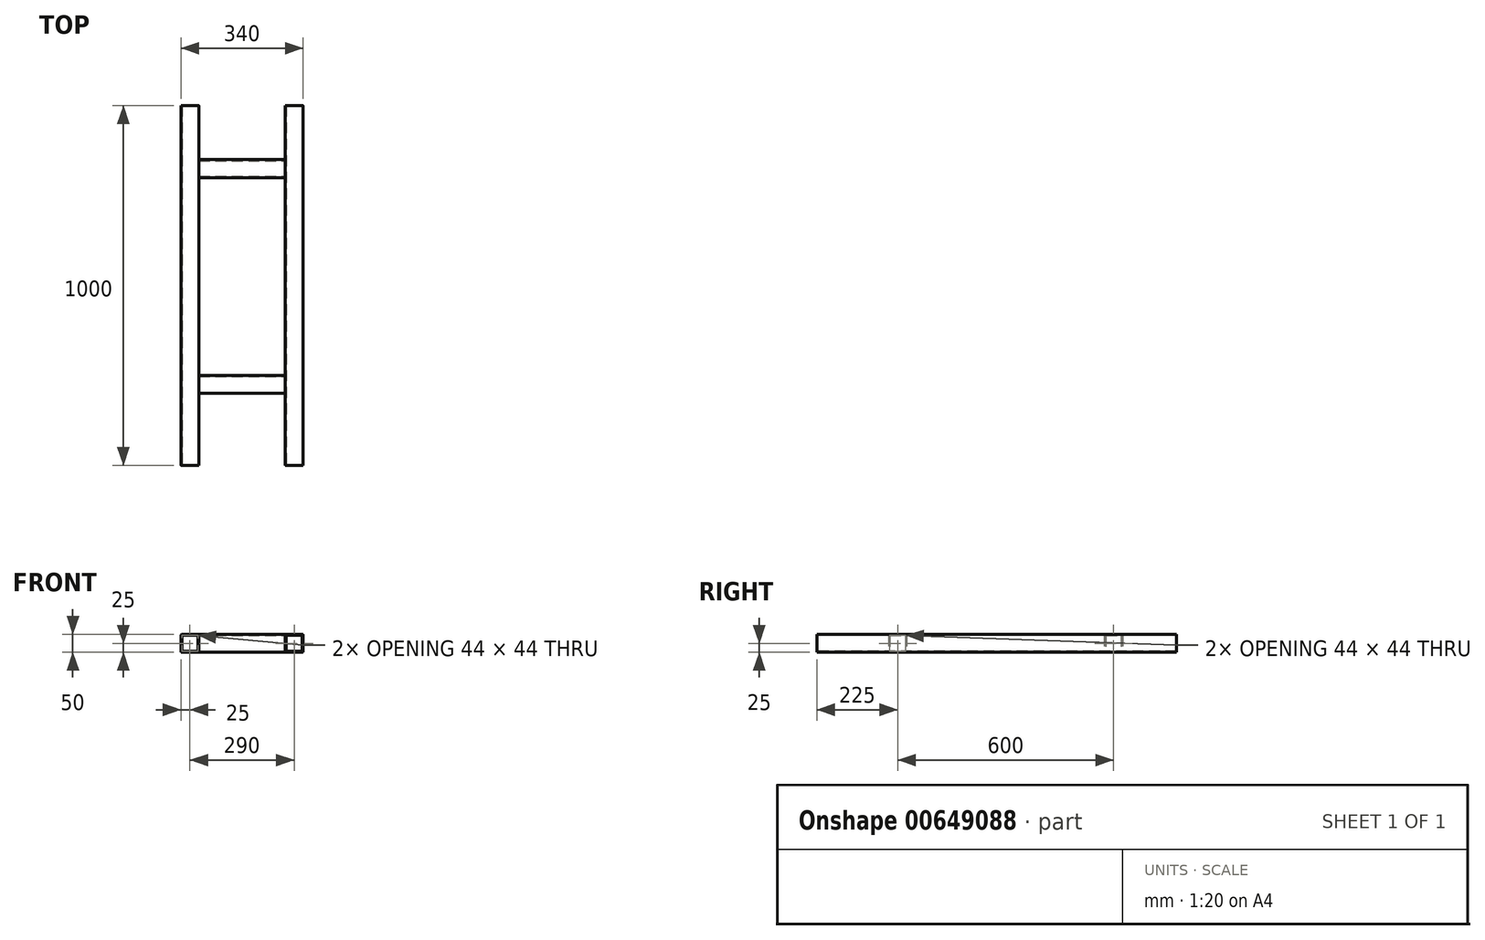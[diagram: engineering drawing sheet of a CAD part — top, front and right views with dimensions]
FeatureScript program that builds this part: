
annotation { "Feature Type Name" : "Feature", "Feature Type Description" : "" }
export const myFeature = defineFeature(function(context is Context, id is Id, definition is map)
    precondition{}
    {
        {
            var Q0;
            Q0=qCreatedBy(makeId("Front.planeOp"),FACE);
            cPlane(context, id + "F0", {"entities" : qUnion([Q0]), "cplaneType" : CPlaneType.OFFSET, "offset" : 500 * mm, "width" : 150 * mm, "height" : 150 * mm});
        }
        {
            var Q0;
            Q0=qCreatedBy(id+"F0.planeOp",FACE);
            var sketch = newSketch(context, id + "F1", { "sketchPlane" : qUnion([Q0])});
            skLineSegment(sketch, "E0.bottom", {"start": v(167, 0) * mm, "end": v(123, 0) * mm});
            skLineSegment(sketch, "E0.top", {"start": v(167, 50) * mm, "end": v(123, 50) * mm});
            skLineSegment(sketch, "E0.left", {"start": v(170, 3) * mm, "end": v(170, 47) * mm});
            skLineSegment(sketch, "E0.right", {"start": v(120, 3) * mm, "end": v(120, 47) * mm});
            skLineSegment(sketch, "E1.bottom", {"start": v(-123, 0) * mm, "end": v(-167, 0) * mm});
            skLineSegment(sketch, "E1.top", {"start": v(-123, 50) * mm, "end": v(-167, 50) * mm});
            skLineSegment(sketch, "E1.left", {"start": v(-120, 3) * mm, "end": v(-120, 47) * mm});
            skLineSegment(sketch, "E1.right", {"start": v(-170, 3) * mm, "end": v(-170, 47) * mm});
            skLineSegment(sketch, "E2.0", {"start": v(-123, 4.5) * mm, "end": v(-123, 45.5) * mm});
            skLineSegment(sketch, "E2.1", {"start": v(-124.5, 3) * mm, "end": v(-165.5, 3) * mm});
            skLineSegment(sketch, "E2.2", {"start": v(-167, 4.5) * mm, "end": v(-167, 45.5) * mm});
            skLineSegment(sketch, "E2.3", {"start": v(-124.5, 47) * mm, "end": v(-165.5, 47) * mm});
            skLineSegment(sketch, "E3.0", {"start": v(165.5, 3) * mm, "end": v(124.5, 3) * mm});
            skLineSegment(sketch, "E3.1", {"start": v(167, 4.5) * mm, "end": v(167, 45.5) * mm});
            skLineSegment(sketch, "E3.2", {"start": v(165.5, 47) * mm, "end": v(124.5, 47) * mm});
            skLineSegment(sketch, "E3.3", {"start": v(123, 4.5) * mm, "end": v(123, 45.5) * mm});
            skPoint(sketch, "E4.visualSharp", {"position": v(120, 50) * mm});
            skArc(sketch, "E4.filletArc", {"start": v(123, 50) * mm, "mid": v(120.88, 49.12) * mm, "end": v(120, 47) * mm});
            skPoint(sketch, "E5.visualSharp", {"position": v(170, 50) * mm});
            skArc(sketch, "E5.filletArc", {"start": v(170, 47) * mm, "mid": v(169.12, 49.12) * mm, "end": v(167, 50) * mm});
            skPoint(sketch, "E6.visualSharp", {"position": v(170, 0) * mm});
            skArc(sketch, "E6.filletArc", {"start": v(167, 0) * mm, "mid": v(169.12, 0.88) * mm, "end": v(170, 3) * mm});
            skPoint(sketch, "E7.visualSharp", {"position": v(120, 0) * mm});
            skArc(sketch, "E7.filletArc", {"start": v(120, 3) * mm, "mid": v(120.88, 0.88) * mm, "end": v(123, 0) * mm});
            skArc(sketch, "E8.filletArc", {"start": v(123, 4.5) * mm, "mid": v(123.44, 3.44) * mm, "end": v(124.5, 3) * mm});
            skArc(sketch, "E9.filletArc", {"start": v(124.5, 47) * mm, "mid": v(123.44, 46.56) * mm, "end": v(123, 45.5) * mm});
            skArc(sketch, "E10.filletArc", {"start": v(167, 45.5) * mm, "mid": v(166.56, 46.56) * mm, "end": v(165.5, 47) * mm});
            skArc(sketch, "E11.filletArc", {"start": v(165.5, 3) * mm, "mid": v(166.56, 3.44) * mm, "end": v(167, 4.5) * mm});
            skPoint(sketch, "E12.visualSharp", {"position": v(-170, 50) * mm});
            skArc(sketch, "E12.filletArc", {"start": v(-167, 50) * mm, "mid": v(-169.12, 49.12) * mm, "end": v(-170, 47) * mm});
            skPoint(sketch, "E13.visualSharp", {"position": v(-120, 50) * mm});
            skArc(sketch, "E13.filletArc", {"start": v(-120, 47) * mm, "mid": v(-120.88, 49.12) * mm, "end": v(-123, 50) * mm});
            skPoint(sketch, "E14.visualSharp", {"position": v(-120, 0) * mm});
            skArc(sketch, "E14.filletArc", {"start": v(-123, 0) * mm, "mid": v(-120.88, 0.88) * mm, "end": v(-120, 3) * mm});
            skPoint(sketch, "E15.visualSharp", {"position": v(-170, 0) * mm});
            skArc(sketch, "E15.filletArc", {"start": v(-170, 3) * mm, "mid": v(-169.12, 0.88) * mm, "end": v(-167, 0) * mm});
            skArc(sketch, "E16.filletArc", {"start": v(-165.5, 47) * mm, "mid": v(-166.56, 46.56) * mm, "end": v(-167, 45.5) * mm});
            skArc(sketch, "E17.filletArc", {"start": v(-123, 45.5) * mm, "mid": v(-123.44, 46.56) * mm, "end": v(-124.5, 47) * mm});
            skArc(sketch, "E18.filletArc", {"start": v(-124.5, 3) * mm, "mid": v(-123.44, 3.44) * mm, "end": v(-123, 4.5) * mm});
            skArc(sketch, "E19.filletArc", {"start": v(-167, 4.5) * mm, "mid": v(-166.56, 3.44) * mm, "end": v(-165.5, 3) * mm});
            skSolve(sketch);
        }
        {
            var Q0;
            Q0=qCreatedBy(makeId("Right.planeOp"),FACE);
            cPlane(context, id + "F2", {"entities" : qUnion([Q0]), "cplaneType" : CPlaneType.OFFSET, "offset" : 120 * mm, "width" : 150 * mm, "height" : 150 * mm});
        }
        {
            var Q0;
            Q0=qCreatedBy(id+"F2.planeOp",FACE);
            var sketch = newSketch(context, id + "F3", { "sketchPlane" : qUnion([Q0])});
            skLineSegment(sketch, "E20.bottom", {"start": v(-297, 50) * mm, "end": v(-253, 50) * mm});
            skLineSegment(sketch, "E20.top", {"start": v(-297, 0) * mm, "end": v(-253, 0) * mm});
            skLineSegment(sketch, "E20.left", {"start": v(-300, 47) * mm, "end": v(-300, 3) * mm});
            skLineSegment(sketch, "E20.right", {"start": v(-250, 47) * mm, "end": v(-250, 3) * mm});
            skLineSegment(sketch, "E21.bottom", {"start": v(303, 50) * mm, "end": v(347, 50) * mm});
            skLineSegment(sketch, "E21.top", {"start": v(303, 0) * mm, "end": v(347, 0) * mm});
            skLineSegment(sketch, "E21.left", {"start": v(300, 47) * mm, "end": v(300, 3) * mm});
            skLineSegment(sketch, "E21.right", {"start": v(350, 47) * mm, "end": v(350, 3) * mm});
            skLineSegment(sketch, "E22.0", {"start": v(-253, 45.5) * mm, "end": v(-253, 4.5) * mm});
            skLineSegment(sketch, "E22.1", {"start": v(-295.5, 47) * mm, "end": v(-254.5, 47) * mm});
            skLineSegment(sketch, "E22.2", {"start": v(-297, 45.5) * mm, "end": v(-297, 4.5) * mm});
            skLineSegment(sketch, "E22.3", {"start": v(-295.5, 3) * mm, "end": v(-254.5, 3) * mm});
            skLineSegment(sketch, "E23.0", {"start": v(303, 45.5) * mm, "end": v(303, 4.5) * mm});
            skLineSegment(sketch, "E23.1", {"start": v(304.5, 47) * mm, "end": v(345.5, 47) * mm});
            skLineSegment(sketch, "E23.2", {"start": v(347, 45.5) * mm, "end": v(347, 4.5) * mm});
            skLineSegment(sketch, "E23.3", {"start": v(304.5, 3) * mm, "end": v(345.5, 3) * mm});
            skPoint(sketch, "E24.visualSharp", {"position": v(-300, 50) * mm});
            skArc(sketch, "E24.filletArc", {"start": v(-297, 50) * mm, "mid": v(-299.12, 49.12) * mm, "end": v(-300, 47) * mm});
            skPoint(sketch, "E25.visualSharp", {"position": v(-250, 50) * mm});
            skArc(sketch, "E25.filletArc", {"start": v(-250, 47) * mm, "mid": v(-250.88, 49.12) * mm, "end": v(-253, 50) * mm});
            skPoint(sketch, "E26.visualSharp", {"position": v(-250, 0) * mm});
            skArc(sketch, "E26.filletArc", {"start": v(-253, 0) * mm, "mid": v(-250.88, 0.88) * mm, "end": v(-250, 3) * mm});
            skPoint(sketch, "E27.visualSharp", {"position": v(-300, 0) * mm});
            skArc(sketch, "E27.filletArc", {"start": v(-300, 3) * mm, "mid": v(-299.12, 0.88) * mm, "end": v(-297, 0) * mm});
            skArc(sketch, "E28.filletArc", {"start": v(-295.5, 47) * mm, "mid": v(-296.56, 46.56) * mm, "end": v(-297, 45.5) * mm});
            skArc(sketch, "E29.filletArc", {"start": v(-253, 45.5) * mm, "mid": v(-253.44, 46.56) * mm, "end": v(-254.5, 47) * mm});
            skArc(sketch, "E30.filletArc", {"start": v(-254.5, 3) * mm, "mid": v(-253.44, 3.44) * mm, "end": v(-253, 4.5) * mm});
            skArc(sketch, "E31.filletArc", {"start": v(-297, 4.5) * mm, "mid": v(-296.56, 3.44) * mm, "end": v(-295.5, 3) * mm});
            skPoint(sketch, "E32.visualSharp", {"position": v(300, 50) * mm});
            skArc(sketch, "E32.filletArc", {"start": v(303, 50) * mm, "mid": v(300.88, 49.12) * mm, "end": v(300, 47) * mm});
            skPoint(sketch, "E33.visualSharp", {"position": v(350, 50) * mm});
            skArc(sketch, "E33.filletArc", {"start": v(350, 47) * mm, "mid": v(349.12, 49.12) * mm, "end": v(347, 50) * mm});
            skPoint(sketch, "E34.visualSharp", {"position": v(350, 0) * mm});
            skArc(sketch, "E34.filletArc", {"start": v(347, 0) * mm, "mid": v(349.12, 0.88) * mm, "end": v(350, 3) * mm});
            skPoint(sketch, "E35.visualSharp", {"position": v(300, 0) * mm});
            skArc(sketch, "E35.filletArc", {"start": v(300, 3) * mm, "mid": v(300.88, 0.88) * mm, "end": v(303, 0) * mm});
            skArc(sketch, "E36.filletArc", {"start": v(304.5, 47) * mm, "mid": v(303.44, 46.56) * mm, "end": v(303, 45.5) * mm});
            skArc(sketch, "E37.filletArc", {"start": v(347, 45.5) * mm, "mid": v(346.56, 46.56) * mm, "end": v(345.5, 47) * mm});
            skArc(sketch, "E38.filletArc", {"start": v(345.5, 3) * mm, "mid": v(346.56, 3.44) * mm, "end": v(347, 4.5) * mm});
            skArc(sketch, "E39.filletArc", {"start": v(303, 4.5) * mm, "mid": v(303.44, 3.44) * mm, "end": v(304.5, 3) * mm});
            skSolve(sketch);
        }
        {
            var Q0;
            Q0=makeQuery(id+"F1.imprint","IMPRINT",FACE,{"disambiguationData":[TD([[makeQuery(id+"F1.imprint","IMPRINT",EDGE,{"derivedFrom":sQuery(id+"F1.wireOp",EDGE,"E1.bottom")}),-1.0]])]});
            var Q1;
            Q1=makeQuery(id+"F1.imprint","IMPRINT",FACE,{"disambiguationData":[TD([[makeQuery(id+"F1.imprint","IMPRINT",EDGE,{"derivedFrom":sQuery(id+"F1.wireOp",EDGE,"E0.bottom")}),-1.0]])]});
            extrude(context, id + "F4", {"entities" : qUnion([Q0, Q1]), "oppositeDirection" : true, "depth" : 1000 * mm, "offsetDistance" : 25 * mm});
        }
        {
            var Q0;
            Q0=makeQuery(id+"F3.imprint","IMPRINT",FACE,{"disambiguationData":[TD([[makeQuery(id+"F3.imprint","IMPRINT",EDGE,{"derivedFrom":sQuery(id+"F3.wireOp",EDGE,"E20.bottom")}),-1.0]])]});
            var Q1;
            Q1=makeQuery(id+"F3.imprint","IMPRINT",FACE,{"disambiguationData":[TD([[makeQuery(id+"F3.imprint","IMPRINT",EDGE,{"derivedFrom":sQuery(id+"F3.wireOp",EDGE,"E21.bottom")}),-1.0]])]});
            extrude(context, id + "F5", {"entities" : qUnion([Q0, Q1]), "oppositeDirection" : true, "depth" : 240 * mm, "offsetDistance" : 25 * mm});
        }
    });
